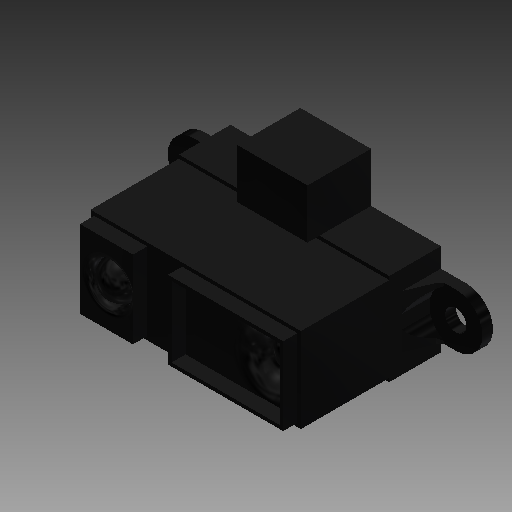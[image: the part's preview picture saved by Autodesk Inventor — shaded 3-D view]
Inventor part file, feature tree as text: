
AUTODESK INVENTOR PART (.ipt)
format: ipt  version: 2017 (Build 210142000, 142)  size: 303,616 bytes
history: native  units: mm
features: sketch x10, extrude x8, projected_geometry x3, chamfer x2, fillet x2, revolve x2, other x1
ambient origin geometry x8: Origin, YZ Plane, XZ Plane, XY Plane, X Axis, Y Axis, Z Axis, Center Point
bodies: Body1 (feature_tree)
feature tree (28):
  other  "솔리드1"
  extrude  "돌출1"  Depth=29.75mm
  extrude  "돌출2"  Depth=13.0mm
  chamfer  "모따기1"  Distance=7.5mm
  chamfer  "모따기2"  Distance=7.5mm
  extrude  "돌출3"  Depth=44.5mm
  extrude  "돌출4"  Depth=3.0mm
  extrude  "돌출5"  Depth=7.3mm TaperAngle=0.0deg
  fillet  "모깎기1"  Radius=5.8mm
  extrude  "돌출6"  Depth=2.0mm TaperAngle=45.0deg
  fillet  "모깎기2"  Radius=2.0mm
  revolve  "회전1"
  revolve  "회전2"
  extrude  "돌출7"  Depth=6.0mm
  extrude  "돌출8"  Depth=14.5mm TaperAngle=0.0deg
  sketch  "스케치1"
  sketch  "스케치2"
  sketch  "스케치3"
  sketch  "스케치4"
  sketch  "스케치5"
  projected_geometry  "투영된 루프1"
  sketch  "스케치6"
  sketch  "스케치7"
  sketch  "스케치8"
  sketch  "스케치9"
  sketch  "스케치10"
  projected_geometry  "투영된 루프2"
  projected_geometry  "투영된 루프3"
